# Revit family: SystemSchroeders_1flg.Tor
name_source: partatom
category: Türen
revit_build: Autodesk Revit 2018 (Build: 20170223_1515(x64)
units: mm (PartAtom-declared; Revit-internal decimal feet)

## family parameters
Basisbauteil = Wand
Beim Laden mit Abzugskörper schneiden = Nein
Gemeinsam genutzt = Nein
Immer vertikal = Ja
OmniClass-Nummer = 23.30.10.00
OmniClass-Titel = Doors
Raumberechnungspunkt = Nein

## types (4) — shared parameters
Abstand Schlupftür = 1620 mm
B02R = 4338 mm
Breite = 2892 mm  [stored 9.48819 ft]
Breite Schiebetor = 2892 mm  [stored 9.48819 ft]
Breite Schlupftür = 1100 mm
Breite Sichtfenster = 350 mm  [stored 1.14829 ft]
Einbauhöhe Sichtfenster = 1500 mm  [stored 4.92126 ft]
Frame Projection Ext. = 25 mm  [stored 0.082021 ft]
Frame Projection Int. = 25 mm  [stored 0.082021 ft]
Frame Width = 75 mm  [stored 0.246063 ft]
Funktion = Innen
Hersteller = System Schröders
Höhe = 3000 mm  [stored 9.84252 ft]
Höhe Griff Schiebetor = 1100 mm
Höhe Griff Schlupftür = 1000 mm  [stored 3.28084 ft]
Höhe Schiebetor = 3000 mm  [stored 9.84252 ft]
Höhe Schlupftür = 2000 mm
Höhe Sichtfenster = 535 mm
T22Hang = 5 mm  [stored 0.0164042 ft]
TsileColumn = 2 mm  [stored 0.00656168 ft]
URL = https://www.system-schroeders.de
Wandabschluss = Nach Basisbauteil
Werkstoff Griff = Edelstahl
Werkstoff Rahmen = Edelstahl Rahmen
Werkstoff Schiebetor = Edelstahl Schiebetor
Werkstoff Schlupftür = Edelstahl Drehtür
Werkstoff Sichtfenster = Glas
mit Sichtfenster = Ja

## per-type parameters (varying)
| type | Feuerschutz | Rauchschutz |
| ST-1 | EI230-Sa-C2 | RS |
| ST-11 | EI290-Sa-C2 | RS |
| RST-1 |  | RS |
| MST-1 |  |  |

note: [stored X ft] marks values corroborated as IEEE doubles in the binary element streams (Revit-internal decimal feet)

## geometry (parser evidence)
native form markers: Sweep x3
no freeform markers — native parametric forms only
